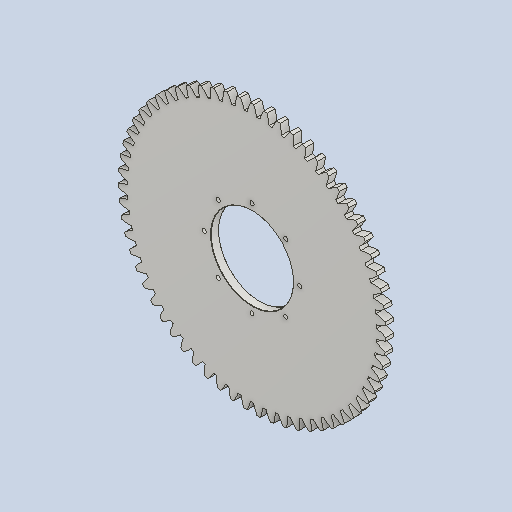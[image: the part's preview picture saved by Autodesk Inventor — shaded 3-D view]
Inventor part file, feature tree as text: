
AUTODESK INVENTOR PART (.ipt)
format: ipt  version: 2025 (Build 290162010, 162A)  size: 899,584 bytes
history: native  units: mm (DEFAULTED — no unit token found)
features: other x4, extrude x3, plane x3, sketch x3, pattern_circular x1, fillet x1, projected_geometry x1
ambient origin geometry x8: Origin, YZ Plane, XZ Plane, XY Plane, X Axis, Y Axis, Z Axis, Center Point
bodies: Solid1 (feature_tree)
feature tree (16):
  extrude  "Extrusion1"  Depth=24.0mm TaperAngle=0.0deg
  plane  "Work Plane2"
  plane  "Work Plane8"
  plane  "Work Plane9"
  other  "Spur Gear"
  extrude  "Extrusion2"  Depth=10.0mm TaperAngle=0.0deg
  extrude  "Extrusion3"  Depth=1.0mm TaperAngle=0.0deg
  pattern_circular  "Circular Pattern1"  [2 undecoded]
  fillet  "Fillet1"  [1 undecoded]
  sketch  "Sketch1"  dims[d0=812.91152mm d1=24.0mm d2=0.0mm]
  other  "Srf1"
  sketch  "Sketch3"  dims[d3=787.89816mm d4=10.0mm d5=0.0mm]
  projected_geometry  "Projected Loop1"
  sketch  "Sketch4"  dims[d16=494.0mm d17=0.0mm d34=0.498666mm d39=0.0mm d41=0.0mm d43=494.0mm d46=494.0mm d47=0.0mm d48=0.0mm d49=250.0mm d50=0.0mm d51=0.0mm d52=12.5mm d53=145.0mm d54=0.0mm d55=0.0mm d56=80.0mm d57=360.0deg d59=1.0mm]
  other  "Pitch Diameter"
  other  "Definition1"
note: 3 required parameter values undecoded (feature->parameter linkage not recoverable at this tier; creation-order binding heuristic only, values carry confidence <= 0.55)
